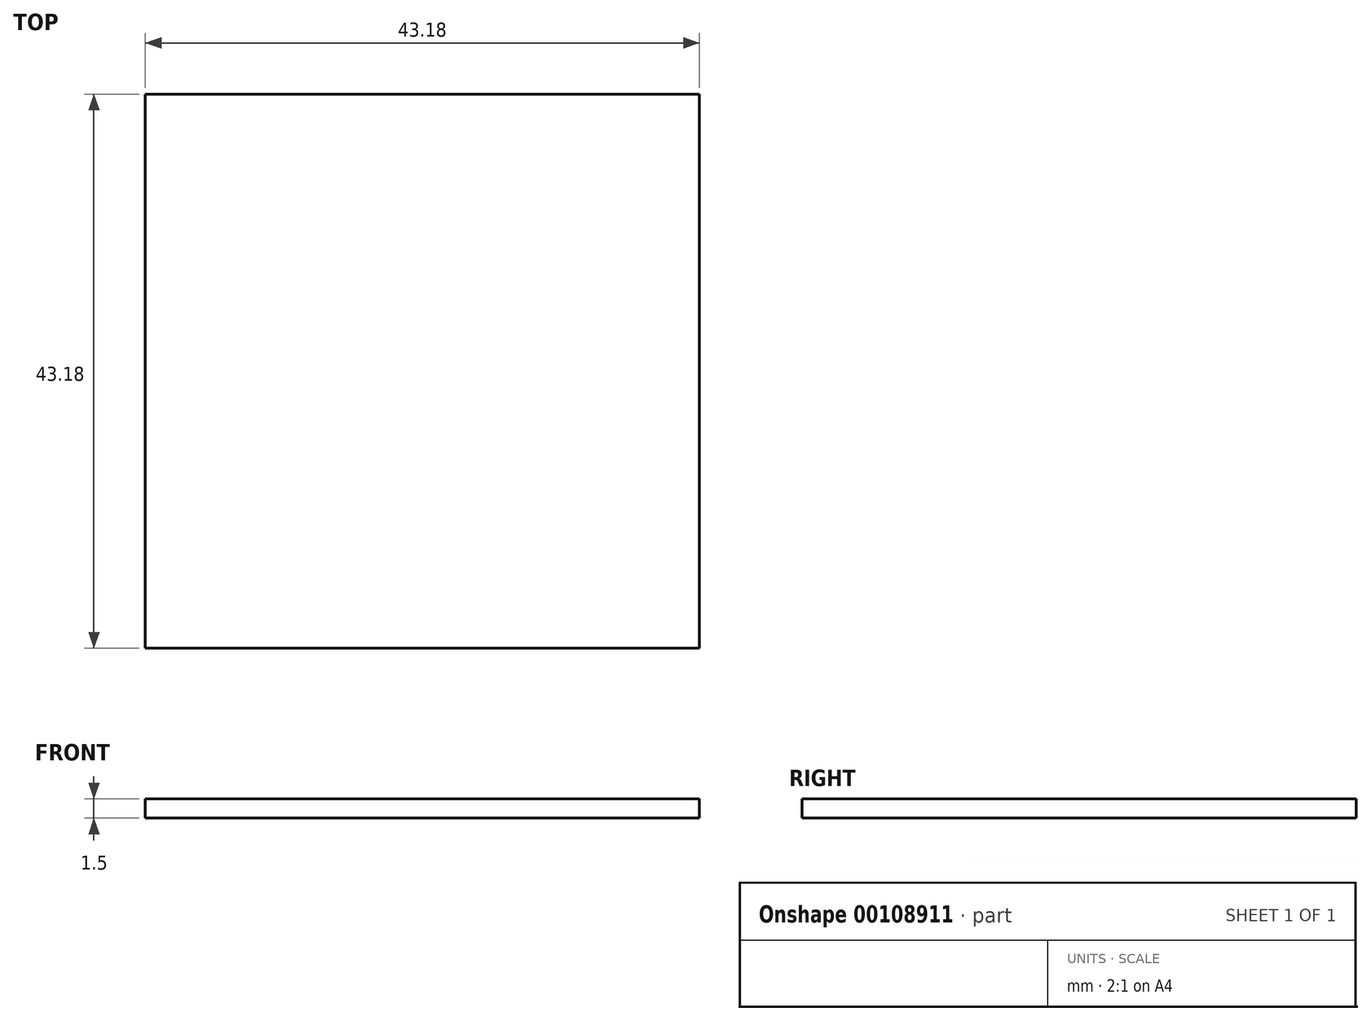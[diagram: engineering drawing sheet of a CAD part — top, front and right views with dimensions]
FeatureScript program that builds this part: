
annotation { "Feature Type Name" : "Feature", "Feature Type Description" : "" }
export const myFeature = defineFeature(function(context is Context, id is Id, definition is map)
    precondition{}
    {
        {
            var Q0;
            Q0=qCreatedBy(makeId("Top.planeOp"),FACE);
            var sketch = newSketch(context, id + "F0", { "sketchPlane" : qUnion([Q0])});
            skLineSegment(sketch, "E0.bottom", {"start": v(-28.84, 29.7) * mm, "end": v(14.34, 29.7) * mm});
            skLineSegment(sketch, "E0.top", {"start": v(-28.84, -13.49) * mm, "end": v(14.34, -13.49) * mm});
            skLineSegment(sketch, "E0.left", {"start": v(-28.84, 29.7) * mm, "end": v(-28.84, -13.49) * mm});
            skLineSegment(sketch, "E0.right", {"start": v(14.34, 29.7) * mm, "end": v(14.34, -13.49) * mm});
            skSolve(sketch);
        }
        {
            var Q0;
            Q0 = qSketchRegion(id + "F0", true);
            extrude(context, id + "F1", {"entities" : qUnion([Q0]), "endBound" : BoundingType.SYMMETRIC, "depth" : 1.5 * mm});
        }
    });
